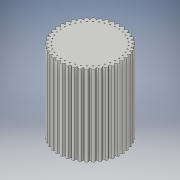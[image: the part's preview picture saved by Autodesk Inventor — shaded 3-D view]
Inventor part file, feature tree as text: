
AUTODESK INVENTOR PART (.ipt)
format: ipt  version: 2019.3 (Build 233278000, 278)  size: 1,217,536 bytes
history: native  units: mm
features: extrude x1
ambient origin geometry x8: Origin, YZ Plane, XZ Plane, XY Plane, X Axis, Y Axis, Z Axis, Center Point
bodies: Body1 (feature_tree)
feature tree (1):
  extrude  "Extrusion2"  Depth=5.047545mm
